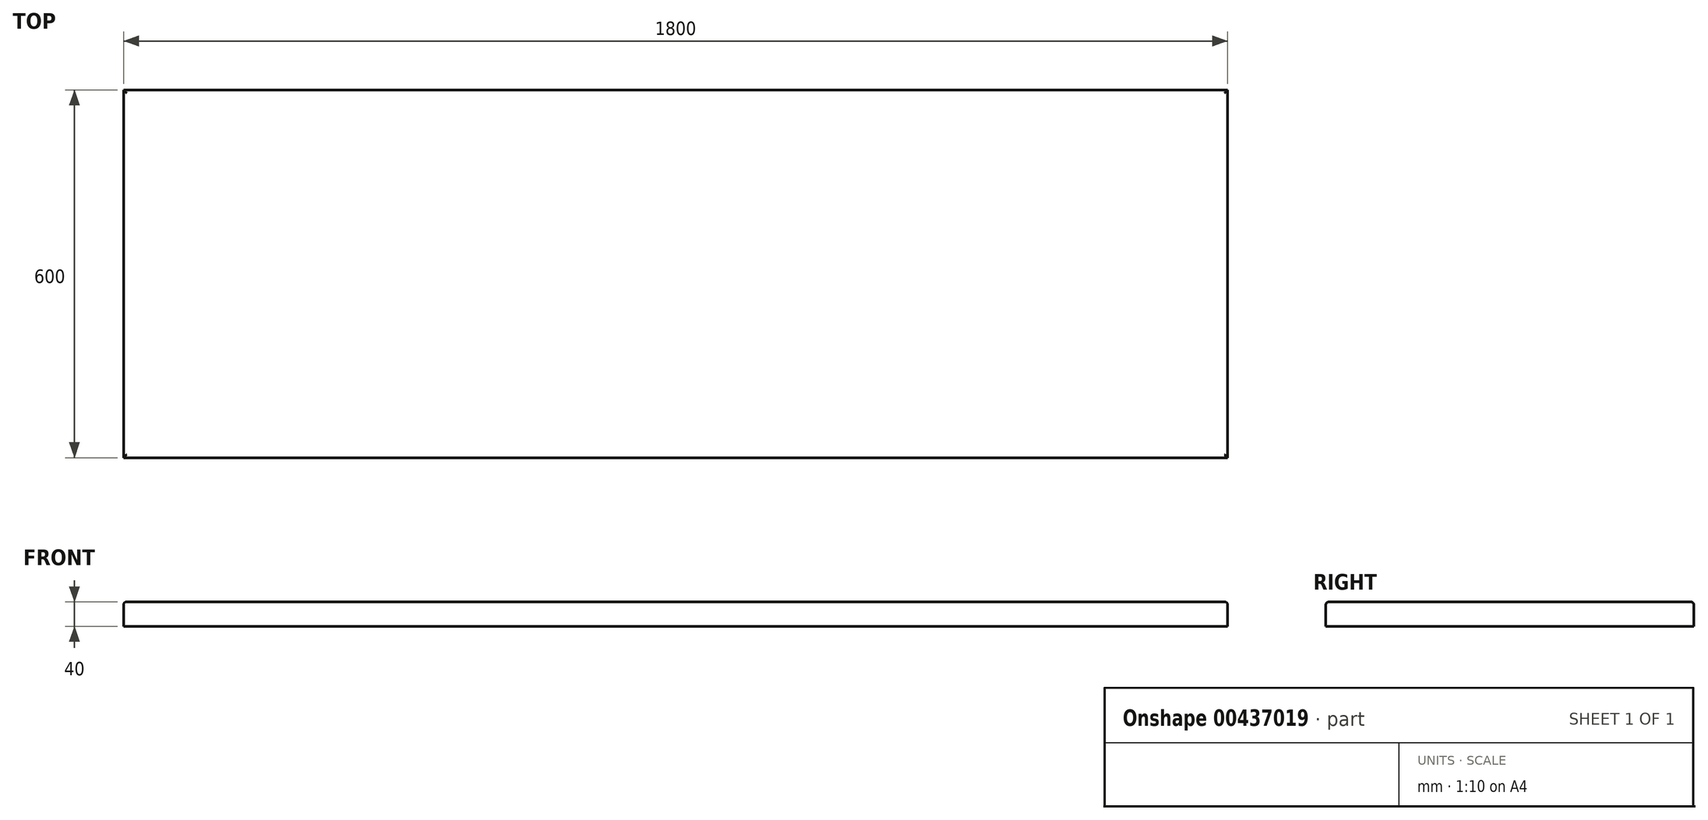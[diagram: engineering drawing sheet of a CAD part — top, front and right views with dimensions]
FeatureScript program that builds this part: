
annotation { "Feature Type Name" : "Feature", "Feature Type Description" : "" }
export const myFeature = defineFeature(function(context is Context, id is Id, definition is map)
    precondition{}
    {
        {
            var Q0;
            Q0=qCreatedBy(makeId("Right.planeOp"),FACE);
            var sketch = newSketch(context, id + "F0", { "sketchPlane" : qUnion([Q0])});
            skLineSegment(sketch, "E0.bottom", {"start": v(0, 0) * mm, "end": v(-600, 0) * mm});
            skLineSegment(sketch, "E0.top", {"start": v(0, 40) * mm, "end": v(-600, 40) * mm});
            skLineSegment(sketch, "E0.left", {"start": v(0, 0) * mm, "end": v(0, 40) * mm});
            skLineSegment(sketch, "E0.right", {"start": v(-600, 0) * mm, "end": v(-600, 40) * mm});
            skSolve(sketch);
        }
        {
            var Q0;
            Q0=qSketchRegion(id+"F0",true);
            extrude(context, id + "F1", {"entities" : qUnion([Q0]), "depth" : 1800 * mm});
        }
        {
            var Q0;
            Q0=makeQuery(id+"F1.opExtrude","SWEPT_FACE",FACE,{"disambiguationData":[OSD([sQuery(id+"F0.wireOp",EDGE,"E0.top")])]});
            fillet(context, id + "F2", {"entities" : qUnion([Q0]), "radius" : 5 * mm, "tangentPropagation" : true, "allowEdgeOverflow" : false});
        }
    });
